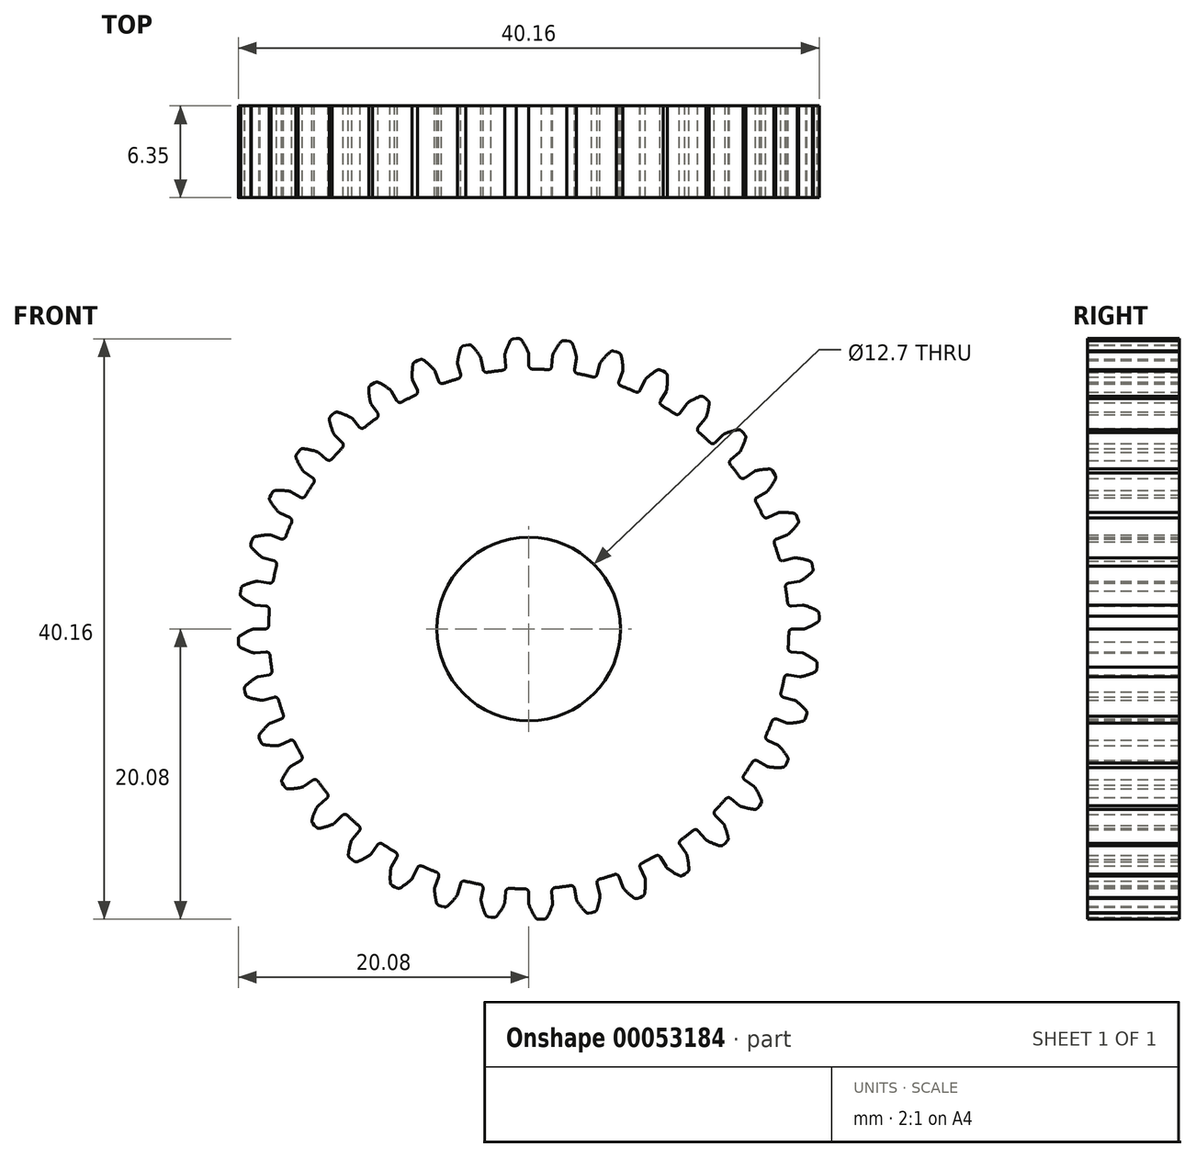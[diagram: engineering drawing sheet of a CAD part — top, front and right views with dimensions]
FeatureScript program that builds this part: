
annotation { "Feature Type Name" : "Feature", "Feature Type Description" : "" }
export const myFeature = defineFeature(function(context is Context, id is Id, definition is map)
    precondition{}
    {
        {
            var Q0;
            Q0=qCreatedBy(makeId("Front.planeOp"),FACE);
            var sketch = newSketch(context, id + "F0", { "sketchPlane" : qUnion([Q0])});
            skArc(sketch, "E0", {"start": v(-1.82, 17.9) * mm, "mid": v(-2.35, 17.83) * mm, "end": v(-2.88, 17.75) * mm});
            skLineSegment(sketch, "E1", {"start": v(0, 18.24) * mm, "end": v(0, 19.05) * mm, "construction": true});
            skLineSegment(sketch, "E2", {"start": v(0, 19) * mm, "end": v(0, 18.24) * mm});
            skLineSegment(sketch, "E3", {"start": v(-0.69, 20.08) * mm, "end": v(-0.88, 20.08) * mm});
            skArc(sketch, "E4.trimOffspring", {"start": v(-0.02, 19.1) * mm, "mid": v(-0.22, 19.54) * mm, "end": v(-0.47, 19.97) * mm});
            skPoint(sketch, "E5.visualSharp", {"position": v(-0.55, 20.08) * mm});
            skArc(sketch, "E5.filletArc", {"start": v(-0.47, 19.97) * mm, "mid": v(-0.56, 20.05) * mm, "end": v(-0.69, 20.08) * mm});
            skPoint(sketch, "E6.visualSharp", {"position": v(0, 19.05) * mm});
            skArc(sketch, "E6.filletArc", {"start": v(0, 19) * mm, "mid": v(0, 19.05) * mm, "end": v(-0.02, 19.1) * mm});
            skLineSegment(sketch, "E7.MirrorCS", {"start": v(-1.07, 20.07) * mm, "end": v(-0.88, 20.08) * mm});
            skLineSegment(sketch, "E8.MirrorCS", {"start": v(-1.66, 18.93) * mm, "end": v(-1.59, 18.17) * mm});
            skArc(sketch, "E9.MirrorCS", {"start": v(-1.66, 18.93) * mm, "mid": v(-1.66, 18.98) * mm, "end": v(-1.65, 19.02) * mm});
            skArc(sketch, "E10.MirrorCS", {"start": v(-1.65, 19.02) * mm, "mid": v(-1.48, 19.49) * mm, "end": v(-1.27, 19.93) * mm});
            skArc(sketch, "E11.MirrorCS", {"start": v(-1.27, 19.93) * mm, "mid": v(-1.18, 20.02) * mm, "end": v(-1.07, 20.07) * mm});
            skPoint(sketch, "E12.visualSharp", {"position": v(0, 17.98) * mm});
            skArc(sketch, "E12.filletArc", {"start": v(0, 18.24) * mm, "mid": v(0.07, 18.06) * mm, "end": v(0.25, 17.98) * mm});
            skPoint(sketch, "E13.visualSharp", {"position": v(-1.57, 17.91) * mm});
            skArc(sketch, "E13.filletArc", {"start": v(-1.82, 17.9) * mm, "mid": v(-1.65, 17.98) * mm, "end": v(-1.59, 18.17) * mm});
            skArc(sketch, "E14.1.0", {"start": v(-4.9, 17.3) * mm, "mid": v(-4.74, 17.42) * mm, "end": v(-4.72, 17.61) * mm});
            skLineSegment(sketch, "E14.1.1", {"start": v(-4.92, 18.35) * mm, "end": v(-4.72, 17.61) * mm});
            skArc(sketch, "E14.1.2", {"start": v(-4.92, 18.35) * mm, "mid": v(-4.93, 18.4) * mm, "end": v(-4.93, 18.45) * mm});
            skArc(sketch, "E14.1.3", {"start": v(-4.93, 18.45) * mm, "mid": v(-4.84, 18.94) * mm, "end": v(-4.71, 19.41) * mm});
            skArc(sketch, "E14.1.4", {"start": v(-4.71, 19.41) * mm, "mid": v(-4.64, 19.51) * mm, "end": v(-4.54, 19.58) * mm});
            skLineSegment(sketch, "E14.1.5", {"start": v(-4.54, 19.58) * mm, "end": v(-4.35, 19.62) * mm});
            skLineSegment(sketch, "E14.1.6", {"start": v(-4.16, 19.66) * mm, "end": v(-4.35, 19.62) * mm});
            skPoint(sketch, "E14.1.7", {"position": v(-4.03, 19.68) * mm});
            skArc(sketch, "E14.1.8", {"start": v(-3.93, 19.58) * mm, "mid": v(-4.04, 19.65) * mm, "end": v(-4.16, 19.66) * mm});
            skArc(sketch, "E14.1.9", {"start": v(-3.33, 18.8) * mm, "mid": v(-3.61, 19.2) * mm, "end": v(-3.93, 19.58) * mm});
            skArc(sketch, "E14.1.10", {"start": v(-3.3, 18.71) * mm, "mid": v(-3.31, 18.76) * mm, "end": v(-3.33, 18.8) * mm});
            skLineSegment(sketch, "E14.1.11", {"start": v(-3.3, 18.71) * mm, "end": v(-3.17, 17.96) * mm});
            skArc(sketch, "E14.1.12", {"start": v(-3.17, 17.96) * mm, "mid": v(-3.06, 17.8) * mm, "end": v(-2.88, 17.75) * mm});
            skArc(sketch, "E14.2.0", {"start": v(-7.83, 16.2) * mm, "mid": v(-7.7, 16.33) * mm, "end": v(-7.7, 16.53) * mm});
            skLineSegment(sketch, "E14.2.1", {"start": v(-8.03, 17.22) * mm, "end": v(-7.7, 16.53) * mm});
            skArc(sketch, "E14.2.2", {"start": v(-8.03, 17.22) * mm, "mid": v(-8.05, 17.27) * mm, "end": v(-8.05, 17.31) * mm});
            skArc(sketch, "E14.2.3", {"start": v(-8.05, 17.31) * mm, "mid": v(-8.06, 17.8) * mm, "end": v(-8, 18.3) * mm});
            skArc(sketch, "E14.2.4", {"start": v(-8, 18.3) * mm, "mid": v(-7.96, 18.41) * mm, "end": v(-7.87, 18.5) * mm});
            skLineSegment(sketch, "E14.2.5", {"start": v(-7.87, 18.5) * mm, "end": v(-7.7, 18.57) * mm});
            skLineSegment(sketch, "E14.2.6", {"start": v(-7.51, 18.64) * mm, "end": v(-7.7, 18.57) * mm});
            skPoint(sketch, "E14.2.7", {"position": v(-7.39, 18.68) * mm});
            skArc(sketch, "E14.2.8", {"start": v(-7.27, 18.6) * mm, "mid": v(-7.39, 18.65) * mm, "end": v(-7.51, 18.64) * mm});
            skArc(sketch, "E14.2.9", {"start": v(-6.55, 17.94) * mm, "mid": v(-6.9, 18.29) * mm, "end": v(-7.27, 18.6) * mm});
            skArc(sketch, "E14.2.10", {"start": v(-6.5, 17.86) * mm, "mid": v(-6.52, 17.9) * mm, "end": v(-6.55, 17.94) * mm});
            skLineSegment(sketch, "E14.2.11", {"start": v(-6.5, 17.86) * mm, "end": v(-6.24, 17.14) * mm});
            skArc(sketch, "E14.2.12", {"start": v(-6.24, 17.14) * mm, "mid": v(-6.1, 17) * mm, "end": v(-5.91, 16.98) * mm});
            skArc(sketch, "E15.2.3.0", {"start": v(-10.52, 14.59) * mm, "mid": v(-10.42, 14.75) * mm, "end": v(-10.46, 14.94) * mm});
            skLineSegment(sketch, "E15.4.3.0", {"start": v(-10.9, 15.57) * mm, "end": v(-10.46, 14.94) * mm});
            skArc(sketch, "E15.7.3.0", {"start": v(-10.9, 15.57) * mm, "mid": v(-10.92, 15.6) * mm, "end": v(-10.94, 15.65) * mm});
            skArc(sketch, "E15.11.3.0", {"start": v(-10.94, 15.65) * mm, "mid": v(-11.03, 16.14) * mm, "end": v(-11.07, 16.63) * mm});
            skArc(sketch, "E15.15.3.0", {"start": v(-11.07, 16.63) * mm, "mid": v(-11.04, 16.75) * mm, "end": v(-10.96, 16.84) * mm});
            skLineSegment(sketch, "E15.19.3.0", {"start": v(-10.96, 16.84) * mm, "end": v(-10.8, 16.95) * mm});
            skLineSegment(sketch, "E15.22.3.0", {"start": v(-10.63, 17.05) * mm, "end": v(-10.8, 16.95) * mm});
            skPoint(sketch, "E15.25.3.0", {"position": v(-10.52, 17.12) * mm});
            skArc(sketch, "E15.26.3.0", {"start": v(-10.4, 17.06) * mm, "mid": v(-10.52, 17.08) * mm, "end": v(-10.63, 17.05) * mm});
            skArc(sketch, "E15.30.3.0", {"start": v(-9.56, 16.53) * mm, "mid": v(-9.97, 16.81) * mm, "end": v(-10.4, 17.06) * mm});
            skArc(sketch, "E15.34.3.0", {"start": v(-9.5, 16.46) * mm, "mid": v(-9.53, 16.5) * mm, "end": v(-9.56, 16.53) * mm});
            skLineSegment(sketch, "E15.38.3.0", {"start": v(-9.5, 16.46) * mm, "end": v(-9.12, 15.8) * mm});
            skArc(sketch, "E15.41.3.0", {"start": v(-9.12, 15.8) * mm, "mid": v(-8.97, 15.67) * mm, "end": v(-8.77, 15.7) * mm});
            skArc(sketch, "E15.2.4.0", {"start": v(-12.9, 12.54) * mm, "mid": v(-12.82, 12.72) * mm, "end": v(-12.9, 12.9) * mm});
            skLineSegment(sketch, "E15.4.4.0", {"start": v(-13.44, 13.44) * mm, "end": v(-12.9, 12.9) * mm});
            skArc(sketch, "E15.7.4.0", {"start": v(-13.44, 13.44) * mm, "mid": v(-13.47, 13.47) * mm, "end": v(-13.5, 13.52) * mm});
            skArc(sketch, "E15.11.4.0", {"start": v(-13.5, 13.52) * mm, "mid": v(-13.66, 13.98) * mm, "end": v(-13.78, 14.45) * mm});
            skArc(sketch, "E15.15.4.0", {"start": v(-13.78, 14.45) * mm, "mid": v(-13.78, 14.58) * mm, "end": v(-13.72, 14.68) * mm});
            skLineSegment(sketch, "E15.19.4.0", {"start": v(-13.72, 14.68) * mm, "end": v(-13.58, 14.82) * mm});
            skLineSegment(sketch, "E15.22.4.0", {"start": v(-13.43, 14.94) * mm, "end": v(-13.58, 14.82) * mm});
            skPoint(sketch, "E15.25.4.0", {"position": v(-13.33, 15.03) * mm});
            skArc(sketch, "E15.26.4.0", {"start": v(-13.2, 15) * mm, "mid": v(-13.32, 15) * mm, "end": v(-13.43, 14.94) * mm});
            skArc(sketch, "E15.30.4.0", {"start": v(-12.29, 14.62) * mm, "mid": v(-12.73, 14.83) * mm, "end": v(-13.2, 15) * mm});
            skArc(sketch, "E15.34.4.0", {"start": v(-12.21, 14.56) * mm, "mid": v(-12.25, 14.6) * mm, "end": v(-12.29, 14.62) * mm});
            skLineSegment(sketch, "E15.38.4.0", {"start": v(-12.21, 14.56) * mm, "end": v(-11.72, 13.97) * mm});
            skArc(sketch, "E15.41.4.0", {"start": v(-11.72, 13.97) * mm, "mid": v(-11.55, 13.88) * mm, "end": v(-11.37, 13.94) * mm});
            skArc(sketch, "E15.2.5.0", {"start": v(-14.87, 10.1) * mm, "mid": v(-14.83, 10.3) * mm, "end": v(-14.94, 10.46) * mm});
            skLineSegment(sketch, "E15.4.5.0", {"start": v(-15.57, 10.9) * mm, "end": v(-14.94, 10.46) * mm});
            skArc(sketch, "E15.7.5.0", {"start": v(-15.57, 10.9) * mm, "mid": v(-15.6, 10.93) * mm, "end": v(-15.63, 10.97) * mm});
            skArc(sketch, "E15.11.5.0", {"start": v(-15.63, 10.97) * mm, "mid": v(-15.88, 11.4) * mm, "end": v(-16.09, 11.84) * mm});
            skArc(sketch, "E15.15.5.0", {"start": v(-16.09, 11.84) * mm, "mid": v(-16.1, 11.96) * mm, "end": v(-16.06, 12.08) * mm});
            skLineSegment(sketch, "E15.19.5.0", {"start": v(-16.06, 12.08) * mm, "end": v(-15.95, 12.24) * mm});
            skLineSegment(sketch, "E15.22.5.0", {"start": v(-15.82, 12.38) * mm, "end": v(-15.95, 12.24) * mm});
            skPoint(sketch, "E15.25.5.0", {"position": v(-15.74, 12.49) * mm});
            skArc(sketch, "E15.26.5.0", {"start": v(-15.6, 12.47) * mm, "mid": v(-15.72, 12.46) * mm, "end": v(-15.82, 12.38) * mm});
            skArc(sketch, "E15.30.5.0", {"start": v(-14.64, 12.26) * mm, "mid": v(-15.11, 12.4) * mm, "end": v(-15.6, 12.47) * mm});
            skArc(sketch, "E15.34.5.0", {"start": v(-14.56, 12.21) * mm, "mid": v(-14.6, 12.24) * mm, "end": v(-14.64, 12.26) * mm});
            skLineSegment(sketch, "E15.38.5.0", {"start": v(-14.56, 12.21) * mm, "end": v(-13.97, 11.72) * mm});
            skArc(sketch, "E15.41.5.0", {"start": v(-13.97, 11.72) * mm, "mid": v(-13.79, 11.66) * mm, "end": v(-13.61, 11.75) * mm});
            skArc(sketch, "E15.2.6.0", {"start": v(-16.4, 7.37) * mm, "mid": v(-16.4, 7.56) * mm, "end": v(-16.53, 7.7) * mm});
            skLineSegment(sketch, "E15.4.6.0", {"start": v(-17.22, 8.03) * mm, "end": v(-16.53, 7.7) * mm});
            skArc(sketch, "E15.7.6.0", {"start": v(-17.22, 8.03) * mm, "mid": v(-17.26, 8.05) * mm, "end": v(-17.3, 8.09) * mm});
            skArc(sketch, "E15.11.6.0", {"start": v(-17.3, 8.09) * mm, "mid": v(-17.62, 8.46) * mm, "end": v(-17.9, 8.87) * mm});
            skArc(sketch, "E15.15.6.0", {"start": v(-17.9, 8.87) * mm, "mid": v(-17.93, 8.99) * mm, "end": v(-17.91, 9.1) * mm});
            skLineSegment(sketch, "E15.19.6.0", {"start": v(-17.91, 9.1) * mm, "end": v(-17.83, 9.28) * mm});
            skLineSegment(sketch, "E15.22.6.0", {"start": v(-17.73, 9.45) * mm, "end": v(-17.83, 9.28) * mm});
            skPoint(sketch, "E15.25.6.0", {"position": v(-17.67, 9.56) * mm});
            skArc(sketch, "E15.26.6.0", {"start": v(-17.53, 9.57) * mm, "mid": v(-17.65, 9.54) * mm, "end": v(-17.73, 9.45) * mm});
            skArc(sketch, "E15.30.6.0", {"start": v(-16.55, 9.53) * mm, "mid": v(-17.04, 9.58) * mm, "end": v(-17.53, 9.57) * mm});
            skArc(sketch, "E15.34.6.0", {"start": v(-16.46, 9.5) * mm, "mid": v(-16.5, 9.52) * mm, "end": v(-16.55, 9.53) * mm});
            skLineSegment(sketch, "E15.38.6.0", {"start": v(-16.46, 9.5) * mm, "end": v(-15.8, 9.12) * mm});
            skArc(sketch, "E15.41.6.0", {"start": v(-15.8, 9.12) * mm, "mid": v(-15.6, 9.1) * mm, "end": v(-15.45, 9.2) * mm});
            skArc(sketch, "E15.2.7.0", {"start": v(-17.43, 4.41) * mm, "mid": v(-17.46, 4.6) * mm, "end": v(-17.61, 4.72) * mm});
            skLineSegment(sketch, "E15.4.7.0", {"start": v(-18.35, 4.92) * mm, "end": v(-17.61, 4.72) * mm});
            skArc(sketch, "E15.7.7.0", {"start": v(-18.35, 4.92) * mm, "mid": v(-18.4, 4.93) * mm, "end": v(-18.44, 4.96) * mm});
            skArc(sketch, "E15.11.7.0", {"start": v(-18.44, 4.96) * mm, "mid": v(-18.82, 5.27) * mm, "end": v(-19.17, 5.63) * mm});
            skArc(sketch, "E15.15.7.0", {"start": v(-19.17, 5.63) * mm, "mid": v(-19.22, 5.74) * mm, "end": v(-19.22, 5.86) * mm});
            skLineSegment(sketch, "E15.19.7.0", {"start": v(-19.22, 5.86) * mm, "end": v(-19.17, 6.04) * mm});
            skLineSegment(sketch, "E15.22.7.0", {"start": v(-19.1, 6.22) * mm, "end": v(-19.17, 6.04) * mm});
            skPoint(sketch, "E15.25.7.0", {"position": v(-19.06, 6.35) * mm});
            skArc(sketch, "E15.26.7.0", {"start": v(-18.93, 6.38) * mm, "mid": v(-19.04, 6.33) * mm, "end": v(-19.1, 6.22) * mm});
            skArc(sketch, "E15.30.7.0", {"start": v(-17.95, 6.51) * mm, "mid": v(-18.44, 6.47) * mm, "end": v(-18.93, 6.38) * mm});
            skArc(sketch, "E15.34.7.0", {"start": v(-17.86, 6.5) * mm, "mid": v(-17.9, 6.51) * mm, "end": v(-17.95, 6.51) * mm});
            skLineSegment(sketch, "E15.38.7.0", {"start": v(-17.86, 6.5) * mm, "end": v(-17.14, 6.24) * mm});
            skArc(sketch, "E15.41.7.0", {"start": v(-17.14, 6.24) * mm, "mid": v(-16.94, 6.24) * mm, "end": v(-16.81, 6.39) * mm});
            skArc(sketch, "E15.2.8.0", {"start": v(-17.93, 1.32) * mm, "mid": v(-18, 1.5) * mm, "end": v(-18.17, 1.59) * mm});
            skLineSegment(sketch, "E15.4.8.0", {"start": v(-18.93, 1.66) * mm, "end": v(-18.17, 1.59) * mm});
            skArc(sketch, "E15.7.8.0", {"start": v(-18.93, 1.66) * mm, "mid": v(-18.98, 1.66) * mm, "end": v(-19.02, 1.68) * mm});
            skArc(sketch, "E15.11.8.0", {"start": v(-19.02, 1.68) * mm, "mid": v(-19.45, 1.93) * mm, "end": v(-19.85, 2.21) * mm});
            skArc(sketch, "E15.15.8.0", {"start": v(-19.85, 2.21) * mm, "mid": v(-19.93, 2.31) * mm, "end": v(-19.95, 2.43) * mm});
            skLineSegment(sketch, "E15.19.8.0", {"start": v(-19.95, 2.43) * mm, "end": v(-19.93, 2.62) * mm});
            skLineSegment(sketch, "E15.22.8.0", {"start": v(-19.9, 2.81) * mm, "end": v(-19.93, 2.62) * mm});
            skPoint(sketch, "E15.25.8.0", {"position": v(-19.87, 2.94) * mm});
            skArc(sketch, "E15.26.8.0", {"start": v(-19.75, 3) * mm, "mid": v(-19.85, 2.93) * mm, "end": v(-19.9, 2.81) * mm});
            skArc(sketch, "E15.30.8.0", {"start": v(-18.8, 3.3) * mm, "mid": v(-19.29, 3.17) * mm, "end": v(-19.75, 3) * mm});
            skArc(sketch, "E15.34.8.0", {"start": v(-18.71, 3.3) * mm, "mid": v(-18.76, 3.3) * mm, "end": v(-18.8, 3.3) * mm});
            skLineSegment(sketch, "E15.38.8.0", {"start": v(-18.71, 3.3) * mm, "end": v(-17.96, 3.17) * mm});
            skArc(sketch, "E15.41.8.0", {"start": v(-17.96, 3.17) * mm, "mid": v(-17.77, 3.2) * mm, "end": v(-17.66, 3.37) * mm});
            skArc(sketch, "E15.2.9.0", {"start": v(-17.9, -1.82) * mm, "mid": v(-17.98, -1.65) * mm, "end": v(-18.17, -1.59) * mm});
            skLineSegment(sketch, "E15.4.9.0", {"start": v(-18.93, -1.66) * mm, "end": v(-18.17, -1.59) * mm});
            skArc(sketch, "E15.7.9.0", {"start": v(-18.93, -1.66) * mm, "mid": v(-18.98, -1.66) * mm, "end": v(-19.02, -1.65) * mm});
            skArc(sketch, "E15.11.9.0", {"start": v(-19.02, -1.65) * mm, "mid": v(-19.49, -1.48) * mm, "end": v(-19.93, -1.27) * mm});
            skArc(sketch, "E15.15.9.0", {"start": v(-19.93, -1.27) * mm, "mid": v(-20.02, -1.18) * mm, "end": v(-20.07, -1.07) * mm});
            skLineSegment(sketch, "E15.19.9.0", {"start": v(-20.07, -1.07) * mm, "end": v(-20.08, -0.88) * mm});
            skLineSegment(sketch, "E15.22.9.0", {"start": v(-20.08, -0.69) * mm, "end": v(-20.08, -0.88) * mm});
            skPoint(sketch, "E15.25.9.0", {"position": v(-20.08, -0.55) * mm});
            skArc(sketch, "E15.26.9.0", {"start": v(-19.97, -0.47) * mm, "mid": v(-20.05, -0.56) * mm, "end": v(-20.08, -0.69) * mm});
            skArc(sketch, "E15.30.9.0", {"start": v(-19.1, -0.02) * mm, "mid": v(-19.54, -0.22) * mm, "end": v(-19.97, -0.47) * mm});
            skArc(sketch, "E15.34.9.0", {"start": v(-19, 0) * mm, "mid": v(-19.05, 0) * mm, "end": v(-19.1, -0.02) * mm});
            skLineSegment(sketch, "E15.38.9.0", {"start": v(-19, 0) * mm, "end": v(-18.24, 0) * mm});
            skArc(sketch, "E15.41.9.0", {"start": v(-18.24, 0) * mm, "mid": v(-18.06, 0.07) * mm, "end": v(-17.98, 0.25) * mm});
            skArc(sketch, "E15.2.10.0", {"start": v(-17.3, -4.9) * mm, "mid": v(-17.42, -4.74) * mm, "end": v(-17.61, -4.72) * mm});
            skLineSegment(sketch, "E15.4.10.0", {"start": v(-18.35, -4.92) * mm, "end": v(-17.61, -4.72) * mm});
            skArc(sketch, "E15.7.10.0", {"start": v(-18.35, -4.92) * mm, "mid": v(-18.4, -4.93) * mm, "end": v(-18.45, -4.93) * mm});
            skArc(sketch, "E15.11.10.0", {"start": v(-18.45, -4.93) * mm, "mid": v(-18.94, -4.84) * mm, "end": v(-19.41, -4.71) * mm});
            skArc(sketch, "E15.15.10.0", {"start": v(-19.41, -4.71) * mm, "mid": v(-19.51, -4.64) * mm, "end": v(-19.58, -4.54) * mm});
            skLineSegment(sketch, "E15.19.10.0", {"start": v(-19.58, -4.54) * mm, "end": v(-19.62, -4.35) * mm});
            skLineSegment(sketch, "E15.22.10.0", {"start": v(-19.66, -4.16) * mm, "end": v(-19.62, -4.35) * mm});
            skPoint(sketch, "E15.25.10.0", {"position": v(-19.68, -4.03) * mm});
            skArc(sketch, "E15.26.10.0", {"start": v(-19.58, -3.93) * mm, "mid": v(-19.65, -4.04) * mm, "end": v(-19.66, -4.16) * mm});
            skArc(sketch, "E15.30.10.0", {"start": v(-18.8, -3.33) * mm, "mid": v(-19.2, -3.61) * mm, "end": v(-19.58, -3.93) * mm});
            skArc(sketch, "E15.34.10.0", {"start": v(-18.71, -3.3) * mm, "mid": v(-18.76, -3.31) * mm, "end": v(-18.8, -3.33) * mm});
            skLineSegment(sketch, "E15.38.10.0", {"start": v(-18.71, -3.3) * mm, "end": v(-17.96, -3.17) * mm});
            skArc(sketch, "E15.41.10.0", {"start": v(-17.96, -3.17) * mm, "mid": v(-17.8, -3.06) * mm, "end": v(-17.75, -2.88) * mm});
            skArc(sketch, "E15.2.11.0", {"start": v(-16.2, -7.83) * mm, "mid": v(-16.33, -7.7) * mm, "end": v(-16.53, -7.7) * mm});
            skLineSegment(sketch, "E15.4.11.0", {"start": v(-17.22, -8.03) * mm, "end": v(-16.53, -7.7) * mm});
            skArc(sketch, "E15.7.11.0", {"start": v(-17.22, -8.03) * mm, "mid": v(-17.27, -8.05) * mm, "end": v(-17.31, -8.05) * mm});
            skArc(sketch, "E15.11.11.0", {"start": v(-17.31, -8.05) * mm, "mid": v(-17.8, -8.06) * mm, "end": v(-18.3, -8) * mm});
            skArc(sketch, "E15.15.11.0", {"start": v(-18.3, -8) * mm, "mid": v(-18.41, -7.96) * mm, "end": v(-18.5, -7.87) * mm});
            skLineSegment(sketch, "E15.19.11.0", {"start": v(-18.5, -7.87) * mm, "end": v(-18.57, -7.7) * mm});
            skLineSegment(sketch, "E15.22.11.0", {"start": v(-18.64, -7.51) * mm, "end": v(-18.57, -7.7) * mm});
            skPoint(sketch, "E15.25.11.0", {"position": v(-18.68, -7.39) * mm});
            skArc(sketch, "E15.26.11.0", {"start": v(-18.6, -7.27) * mm, "mid": v(-18.65, -7.39) * mm, "end": v(-18.64, -7.51) * mm});
            skArc(sketch, "E15.30.11.0", {"start": v(-17.94, -6.55) * mm, "mid": v(-18.29, -6.9) * mm, "end": v(-18.6, -7.27) * mm});
            skArc(sketch, "E15.34.11.0", {"start": v(-17.86, -6.5) * mm, "mid": v(-17.9, -6.52) * mm, "end": v(-17.94, -6.55) * mm});
            skLineSegment(sketch, "E15.38.11.0", {"start": v(-17.86, -6.5) * mm, "end": v(-17.14, -6.24) * mm});
            skArc(sketch, "E15.41.11.0", {"start": v(-17.14, -6.24) * mm, "mid": v(-17, -6.1) * mm, "end": v(-16.98, -5.91) * mm});
            skArc(sketch, "E15.2.12.0", {"start": v(-14.59, -10.52) * mm, "mid": v(-14.75, -10.42) * mm, "end": v(-14.94, -10.46) * mm});
            skLineSegment(sketch, "E15.4.12.0", {"start": v(-15.57, -10.9) * mm, "end": v(-14.94, -10.46) * mm});
            skArc(sketch, "E15.7.12.0", {"start": v(-15.57, -10.9) * mm, "mid": v(-15.6, -10.92) * mm, "end": v(-15.65, -10.94) * mm});
            skArc(sketch, "E15.11.12.0", {"start": v(-15.65, -10.94) * mm, "mid": v(-16.14, -11.03) * mm, "end": v(-16.63, -11.07) * mm});
            skArc(sketch, "E15.15.12.0", {"start": v(-16.63, -11.07) * mm, "mid": v(-16.75, -11.04) * mm, "end": v(-16.84, -10.96) * mm});
            skLineSegment(sketch, "E15.19.12.0", {"start": v(-16.84, -10.96) * mm, "end": v(-16.95, -10.8) * mm});
            skLineSegment(sketch, "E15.22.12.0", {"start": v(-17.05, -10.63) * mm, "end": v(-16.95, -10.8) * mm});
            skPoint(sketch, "E15.25.12.0", {"position": v(-17.12, -10.52) * mm});
            skArc(sketch, "E15.26.12.0", {"start": v(-17.06, -10.4) * mm, "mid": v(-17.08, -10.52) * mm, "end": v(-17.05, -10.63) * mm});
            skArc(sketch, "E15.30.12.0", {"start": v(-16.53, -9.56) * mm, "mid": v(-16.81, -9.97) * mm, "end": v(-17.06, -10.4) * mm});
            skArc(sketch, "E15.34.12.0", {"start": v(-16.46, -9.5) * mm, "mid": v(-16.5, -9.53) * mm, "end": v(-16.53, -9.56) * mm});
            skLineSegment(sketch, "E15.38.12.0", {"start": v(-16.46, -9.5) * mm, "end": v(-15.8, -9.12) * mm});
            skArc(sketch, "E15.41.12.0", {"start": v(-15.8, -9.12) * mm, "mid": v(-15.67, -8.97) * mm, "end": v(-15.7, -8.77) * mm});
            skArc(sketch, "E15.2.13.0", {"start": v(-12.54, -12.9) * mm, "mid": v(-12.72, -12.82) * mm, "end": v(-12.9, -12.9) * mm});
            skLineSegment(sketch, "E15.4.13.0", {"start": v(-13.44, -13.44) * mm, "end": v(-12.9, -12.9) * mm});
            skArc(sketch, "E15.7.13.0", {"start": v(-13.44, -13.44) * mm, "mid": v(-13.47, -13.47) * mm, "end": v(-13.52, -13.5) * mm});
            skArc(sketch, "E15.11.13.0", {"start": v(-13.52, -13.5) * mm, "mid": v(-13.98, -13.66) * mm, "end": v(-14.45, -13.78) * mm});
            skArc(sketch, "E15.15.13.0", {"start": v(-14.45, -13.78) * mm, "mid": v(-14.58, -13.78) * mm, "end": v(-14.68, -13.72) * mm});
            skLineSegment(sketch, "E15.19.13.0", {"start": v(-14.68, -13.72) * mm, "end": v(-14.82, -13.58) * mm});
            skLineSegment(sketch, "E15.22.13.0", {"start": v(-14.94, -13.43) * mm, "end": v(-14.82, -13.58) * mm});
            skPoint(sketch, "E15.25.13.0", {"position": v(-15.03, -13.33) * mm});
            skArc(sketch, "E15.26.13.0", {"start": v(-15, -13.2) * mm, "mid": v(-15, -13.32) * mm, "end": v(-14.94, -13.43) * mm});
            skArc(sketch, "E15.30.13.0", {"start": v(-14.62, -12.29) * mm, "mid": v(-14.83, -12.73) * mm, "end": v(-15, -13.2) * mm});
            skArc(sketch, "E15.34.13.0", {"start": v(-14.56, -12.21) * mm, "mid": v(-14.6, -12.25) * mm, "end": v(-14.62, -12.29) * mm});
            skLineSegment(sketch, "E15.38.13.0", {"start": v(-14.56, -12.21) * mm, "end": v(-13.97, -11.72) * mm});
            skArc(sketch, "E15.41.13.0", {"start": v(-13.97, -11.72) * mm, "mid": v(-13.88, -11.55) * mm, "end": v(-13.94, -11.37) * mm});
            skArc(sketch, "E15.2.14.0", {"start": v(-10.1, -14.87) * mm, "mid": v(-10.3, -14.83) * mm, "end": v(-10.46, -14.94) * mm});
            skLineSegment(sketch, "E15.4.14.0", {"start": v(-10.9, -15.57) * mm, "end": v(-10.46, -14.94) * mm});
            skArc(sketch, "E15.7.14.0", {"start": v(-10.9, -15.57) * mm, "mid": v(-10.93, -15.6) * mm, "end": v(-10.97, -15.63) * mm});
            skArc(sketch, "E15.11.14.0", {"start": v(-10.97, -15.63) * mm, "mid": v(-11.4, -15.88) * mm, "end": v(-11.84, -16.09) * mm});
            skArc(sketch, "E15.15.14.0", {"start": v(-11.84, -16.09) * mm, "mid": v(-11.96, -16.1) * mm, "end": v(-12.08, -16.06) * mm});
            skLineSegment(sketch, "E15.19.14.0", {"start": v(-12.08, -16.06) * mm, "end": v(-12.24, -15.95) * mm});
            skLineSegment(sketch, "E15.22.14.0", {"start": v(-12.38, -15.82) * mm, "end": v(-12.24, -15.95) * mm});
            skPoint(sketch, "E15.25.14.0", {"position": v(-12.49, -15.74) * mm});
            skArc(sketch, "E15.26.14.0", {"start": v(-12.47, -15.6) * mm, "mid": v(-12.46, -15.72) * mm, "end": v(-12.38, -15.82) * mm});
            skArc(sketch, "E15.30.14.0", {"start": v(-12.26, -14.64) * mm, "mid": v(-12.4, -15.11) * mm, "end": v(-12.47, -15.6) * mm});
            skArc(sketch, "E15.34.14.0", {"start": v(-12.21, -14.56) * mm, "mid": v(-12.24, -14.6) * mm, "end": v(-12.26, -14.64) * mm});
            skLineSegment(sketch, "E15.38.14.0", {"start": v(-12.21, -14.56) * mm, "end": v(-11.72, -13.97) * mm});
            skArc(sketch, "E15.41.14.0", {"start": v(-11.72, -13.97) * mm, "mid": v(-11.66, -13.79) * mm, "end": v(-11.75, -13.61) * mm});
            skArc(sketch, "E15.2.15.0", {"start": v(-7.37, -16.4) * mm, "mid": v(-7.56, -16.4) * mm, "end": v(-7.7, -16.53) * mm});
            skLineSegment(sketch, "E15.4.15.0", {"start": v(-8.03, -17.22) * mm, "end": v(-7.7, -16.53) * mm});
            skArc(sketch, "E15.7.15.0", {"start": v(-8.03, -17.22) * mm, "mid": v(-8.05, -17.26) * mm, "end": v(-8.09, -17.3) * mm});
            skArc(sketch, "E15.11.15.0", {"start": v(-8.09, -17.3) * mm, "mid": v(-8.46, -17.62) * mm, "end": v(-8.87, -17.9) * mm});
            skArc(sketch, "E15.15.15.0", {"start": v(-8.87, -17.9) * mm, "mid": v(-8.99, -17.93) * mm, "end": v(-9.1, -17.91) * mm});
            skLineSegment(sketch, "E15.19.15.0", {"start": v(-9.1, -17.91) * mm, "end": v(-9.28, -17.83) * mm});
            skLineSegment(sketch, "E15.22.15.0", {"start": v(-9.45, -17.73) * mm, "end": v(-9.28, -17.83) * mm});
            skPoint(sketch, "E15.25.15.0", {"position": v(-9.56, -17.67) * mm});
            skArc(sketch, "E15.26.15.0", {"start": v(-9.57, -17.53) * mm, "mid": v(-9.54, -17.65) * mm, "end": v(-9.45, -17.73) * mm});
            skArc(sketch, "E15.30.15.0", {"start": v(-9.53, -16.55) * mm, "mid": v(-9.58, -17.04) * mm, "end": v(-9.57, -17.53) * mm});
            skArc(sketch, "E15.34.15.0", {"start": v(-9.5, -16.46) * mm, "mid": v(-9.52, -16.5) * mm, "end": v(-9.53, -16.55) * mm});
            skLineSegment(sketch, "E15.38.15.0", {"start": v(-9.5, -16.46) * mm, "end": v(-9.12, -15.8) * mm});
            skArc(sketch, "E15.41.15.0", {"start": v(-9.12, -15.8) * mm, "mid": v(-9.1, -15.6) * mm, "end": v(-9.2, -15.45) * mm});
            skArc(sketch, "E15.2.16.0", {"start": v(-4.41, -17.43) * mm, "mid": v(-4.6, -17.46) * mm, "end": v(-4.72, -17.61) * mm});
            skLineSegment(sketch, "E15.4.16.0", {"start": v(-4.92, -18.35) * mm, "end": v(-4.72, -17.61) * mm});
            skArc(sketch, "E15.7.16.0", {"start": v(-4.92, -18.35) * mm, "mid": v(-4.93, -18.4) * mm, "end": v(-4.96, -18.44) * mm});
            skArc(sketch, "E15.11.16.0", {"start": v(-4.96, -18.44) * mm, "mid": v(-5.27, -18.82) * mm, "end": v(-5.63, -19.17) * mm});
            skArc(sketch, "E15.15.16.0", {"start": v(-5.63, -19.17) * mm, "mid": v(-5.74, -19.22) * mm, "end": v(-5.86, -19.22) * mm});
            skLineSegment(sketch, "E15.19.16.0", {"start": v(-5.86, -19.22) * mm, "end": v(-6.04, -19.17) * mm});
            skLineSegment(sketch, "E15.22.16.0", {"start": v(-6.22, -19.1) * mm, "end": v(-6.04, -19.17) * mm});
            skPoint(sketch, "E15.25.16.0", {"position": v(-6.35, -19.06) * mm});
            skArc(sketch, "E15.26.16.0", {"start": v(-6.38, -18.93) * mm, "mid": v(-6.33, -19.04) * mm, "end": v(-6.22, -19.1) * mm});
            skArc(sketch, "E15.30.16.0", {"start": v(-6.51, -17.95) * mm, "mid": v(-6.47, -18.44) * mm, "end": v(-6.38, -18.93) * mm});
            skArc(sketch, "E15.34.16.0", {"start": v(-6.5, -17.86) * mm, "mid": v(-6.51, -17.9) * mm, "end": v(-6.51, -17.95) * mm});
            skLineSegment(sketch, "E15.38.16.0", {"start": v(-6.5, -17.86) * mm, "end": v(-6.24, -17.14) * mm});
            skArc(sketch, "E15.41.16.0", {"start": v(-6.24, -17.14) * mm, "mid": v(-6.24, -16.94) * mm, "end": v(-6.39, -16.81) * mm});
            skArc(sketch, "E15.2.17.0", {"start": v(-1.32, -17.93) * mm, "mid": v(-1.5, -18) * mm, "end": v(-1.59, -18.17) * mm});
            skLineSegment(sketch, "E15.4.17.0", {"start": v(-1.66, -18.93) * mm, "end": v(-1.59, -18.17) * mm});
            skArc(sketch, "E15.7.17.0", {"start": v(-1.66, -18.93) * mm, "mid": v(-1.66, -18.98) * mm, "end": v(-1.68, -19.02) * mm});
            skArc(sketch, "E15.11.17.0", {"start": v(-1.68, -19.02) * mm, "mid": v(-1.93, -19.45) * mm, "end": v(-2.21, -19.85) * mm});
            skArc(sketch, "E15.15.17.0", {"start": v(-2.21, -19.85) * mm, "mid": v(-2.31, -19.93) * mm, "end": v(-2.43, -19.95) * mm});
            skLineSegment(sketch, "E15.19.17.0", {"start": v(-2.43, -19.95) * mm, "end": v(-2.62, -19.93) * mm});
            skLineSegment(sketch, "E15.22.17.0", {"start": v(-2.81, -19.9) * mm, "end": v(-2.62, -19.93) * mm});
            skPoint(sketch, "E15.25.17.0", {"position": v(-2.94, -19.87) * mm});
            skArc(sketch, "E15.26.17.0", {"start": v(-3, -19.75) * mm, "mid": v(-2.93, -19.85) * mm, "end": v(-2.81, -19.9) * mm});
            skArc(sketch, "E15.30.17.0", {"start": v(-3.3, -18.8) * mm, "mid": v(-3.17, -19.29) * mm, "end": v(-3, -19.75) * mm});
            skArc(sketch, "E15.34.17.0", {"start": v(-3.3, -18.71) * mm, "mid": v(-3.3, -18.76) * mm, "end": v(-3.3, -18.8) * mm});
            skLineSegment(sketch, "E15.38.17.0", {"start": v(-3.3, -18.71) * mm, "end": v(-3.17, -17.96) * mm});
            skArc(sketch, "E15.41.17.0", {"start": v(-3.17, -17.96) * mm, "mid": v(-3.2, -17.77) * mm, "end": v(-3.37, -17.66) * mm});
            skArc(sketch, "E15.2.18.0", {"start": v(1.82, -17.9) * mm, "mid": v(1.65, -17.98) * mm, "end": v(1.59, -18.17) * mm});
            skLineSegment(sketch, "E15.4.18.0", {"start": v(1.66, -18.93) * mm, "end": v(1.59, -18.17) * mm});
            skArc(sketch, "E15.7.18.0", {"start": v(1.66, -18.93) * mm, "mid": v(1.66, -18.98) * mm, "end": v(1.65, -19.02) * mm});
            skArc(sketch, "E15.11.18.0", {"start": v(1.65, -19.02) * mm, "mid": v(1.48, -19.49) * mm, "end": v(1.27, -19.93) * mm});
            skArc(sketch, "E15.15.18.0", {"start": v(1.27, -19.93) * mm, "mid": v(1.18, -20.02) * mm, "end": v(1.07, -20.07) * mm});
            skLineSegment(sketch, "E15.19.18.0", {"start": v(1.07, -20.07) * mm, "end": v(0.88, -20.08) * mm});
            skLineSegment(sketch, "E15.22.18.0", {"start": v(0.69, -20.08) * mm, "end": v(0.88, -20.08) * mm});
            skPoint(sketch, "E15.25.18.0", {"position": v(0.55, -20.08) * mm});
            skArc(sketch, "E15.26.18.0", {"start": v(0.47, -19.97) * mm, "mid": v(0.56, -20.05) * mm, "end": v(0.69, -20.08) * mm});
            skArc(sketch, "E15.30.18.0", {"start": v(0.02, -19.1) * mm, "mid": v(0.22, -19.54) * mm, "end": v(0.47, -19.97) * mm});
            skArc(sketch, "E15.34.18.0", {"start": v(0, -19) * mm, "mid": v(0, -19.05) * mm, "end": v(0.02, -19.1) * mm});
            skLineSegment(sketch, "E15.38.18.0", {"start": v(0, -19) * mm, "end": v(0, -18.24) * mm});
            skArc(sketch, "E15.41.18.0", {"start": v(0, -18.24) * mm, "mid": v(-0.07, -18.06) * mm, "end": v(-0.25, -17.98) * mm});
            skArc(sketch, "E15.2.19.0", {"start": v(4.9, -17.3) * mm, "mid": v(4.74, -17.42) * mm, "end": v(4.72, -17.61) * mm});
            skLineSegment(sketch, "E15.4.19.0", {"start": v(4.92, -18.35) * mm, "end": v(4.72, -17.61) * mm});
            skArc(sketch, "E15.7.19.0", {"start": v(4.92, -18.35) * mm, "mid": v(4.93, -18.4) * mm, "end": v(4.93, -18.45) * mm});
            skArc(sketch, "E15.11.19.0", {"start": v(4.93, -18.45) * mm, "mid": v(4.84, -18.94) * mm, "end": v(4.71, -19.41) * mm});
            skArc(sketch, "E15.15.19.0", {"start": v(4.71, -19.41) * mm, "mid": v(4.64, -19.51) * mm, "end": v(4.54, -19.58) * mm});
            skLineSegment(sketch, "E15.19.19.0", {"start": v(4.54, -19.58) * mm, "end": v(4.35, -19.62) * mm});
            skLineSegment(sketch, "E15.22.19.0", {"start": v(4.16, -19.66) * mm, "end": v(4.35, -19.62) * mm});
            skPoint(sketch, "E15.25.19.0", {"position": v(4.03, -19.68) * mm});
            skArc(sketch, "E15.26.19.0", {"start": v(3.93, -19.58) * mm, "mid": v(4.04, -19.65) * mm, "end": v(4.16, -19.66) * mm});
            skArc(sketch, "E15.30.19.0", {"start": v(3.33, -18.8) * mm, "mid": v(3.61, -19.2) * mm, "end": v(3.93, -19.58) * mm});
            skArc(sketch, "E15.34.19.0", {"start": v(3.3, -18.71) * mm, "mid": v(3.31, -18.76) * mm, "end": v(3.33, -18.8) * mm});
            skLineSegment(sketch, "E15.38.19.0", {"start": v(3.3, -18.71) * mm, "end": v(3.17, -17.96) * mm});
            skArc(sketch, "E15.41.19.0", {"start": v(3.17, -17.96) * mm, "mid": v(3.06, -17.8) * mm, "end": v(2.88, -17.75) * mm});
            skArc(sketch, "E15.2.20.0", {"start": v(7.83, -16.2) * mm, "mid": v(7.7, -16.33) * mm, "end": v(7.7, -16.53) * mm});
            skLineSegment(sketch, "E15.4.20.0", {"start": v(8.03, -17.22) * mm, "end": v(7.7, -16.53) * mm});
            skArc(sketch, "E15.7.20.0", {"start": v(8.03, -17.22) * mm, "mid": v(8.05, -17.27) * mm, "end": v(8.05, -17.31) * mm});
            skArc(sketch, "E15.11.20.0", {"start": v(8.05, -17.31) * mm, "mid": v(8.06, -17.8) * mm, "end": v(8, -18.3) * mm});
            skArc(sketch, "E15.15.20.0", {"start": v(8, -18.3) * mm, "mid": v(7.96, -18.41) * mm, "end": v(7.87, -18.5) * mm});
            skLineSegment(sketch, "E15.19.20.0", {"start": v(7.87, -18.5) * mm, "end": v(7.7, -18.57) * mm});
            skLineSegment(sketch, "E15.22.20.0", {"start": v(7.51, -18.64) * mm, "end": v(7.7, -18.57) * mm});
            skPoint(sketch, "E15.25.20.0", {"position": v(7.39, -18.68) * mm});
            skArc(sketch, "E15.26.20.0", {"start": v(7.27, -18.6) * mm, "mid": v(7.39, -18.65) * mm, "end": v(7.51, -18.64) * mm});
            skArc(sketch, "E15.30.20.0", {"start": v(6.55, -17.94) * mm, "mid": v(6.9, -18.29) * mm, "end": v(7.27, -18.6) * mm});
            skArc(sketch, "E15.34.20.0", {"start": v(6.5, -17.86) * mm, "mid": v(6.52, -17.9) * mm, "end": v(6.55, -17.94) * mm});
            skLineSegment(sketch, "E15.38.20.0", {"start": v(6.5, -17.86) * mm, "end": v(6.24, -17.14) * mm});
            skArc(sketch, "E15.41.20.0", {"start": v(6.24, -17.14) * mm, "mid": v(6.1, -17) * mm, "end": v(5.91, -16.98) * mm});
            skArc(sketch, "E15.2.21.0", {"start": v(10.52, -14.59) * mm, "mid": v(10.42, -14.75) * mm, "end": v(10.46, -14.94) * mm});
            skLineSegment(sketch, "E15.4.21.0", {"start": v(10.9, -15.57) * mm, "end": v(10.46, -14.94) * mm});
            skArc(sketch, "E15.7.21.0", {"start": v(10.9, -15.57) * mm, "mid": v(10.92, -15.6) * mm, "end": v(10.94, -15.65) * mm});
            skArc(sketch, "E15.11.21.0", {"start": v(10.94, -15.65) * mm, "mid": v(11.03, -16.14) * mm, "end": v(11.07, -16.63) * mm});
            skArc(sketch, "E15.15.21.0", {"start": v(11.07, -16.63) * mm, "mid": v(11.04, -16.75) * mm, "end": v(10.96, -16.84) * mm});
            skLineSegment(sketch, "E15.19.21.0", {"start": v(10.96, -16.84) * mm, "end": v(10.8, -16.95) * mm});
            skLineSegment(sketch, "E15.22.21.0", {"start": v(10.63, -17.05) * mm, "end": v(10.8, -16.95) * mm});
            skPoint(sketch, "E15.25.21.0", {"position": v(10.52, -17.12) * mm});
            skArc(sketch, "E15.26.21.0", {"start": v(10.4, -17.06) * mm, "mid": v(10.52, -17.08) * mm, "end": v(10.63, -17.05) * mm});
            skArc(sketch, "E15.30.21.0", {"start": v(9.56, -16.53) * mm, "mid": v(9.97, -16.81) * mm, "end": v(10.4, -17.06) * mm});
            skArc(sketch, "E15.34.21.0", {"start": v(9.5, -16.46) * mm, "mid": v(9.53, -16.5) * mm, "end": v(9.56, -16.53) * mm});
            skLineSegment(sketch, "E15.38.21.0", {"start": v(9.5, -16.46) * mm, "end": v(9.12, -15.8) * mm});
            skArc(sketch, "E15.41.21.0", {"start": v(9.12, -15.8) * mm, "mid": v(8.97, -15.67) * mm, "end": v(8.77, -15.7) * mm});
            skArc(sketch, "E15.2.22.0", {"start": v(12.9, -12.54) * mm, "mid": v(12.82, -12.72) * mm, "end": v(12.9, -12.9) * mm});
            skLineSegment(sketch, "E15.4.22.0", {"start": v(13.44, -13.44) * mm, "end": v(12.9, -12.9) * mm});
            skArc(sketch, "E15.7.22.0", {"start": v(13.44, -13.44) * mm, "mid": v(13.47, -13.47) * mm, "end": v(13.5, -13.52) * mm});
            skArc(sketch, "E15.11.22.0", {"start": v(13.5, -13.52) * mm, "mid": v(13.66, -13.98) * mm, "end": v(13.78, -14.45) * mm});
            skArc(sketch, "E15.15.22.0", {"start": v(13.78, -14.45) * mm, "mid": v(13.78, -14.58) * mm, "end": v(13.72, -14.68) * mm});
            skLineSegment(sketch, "E15.19.22.0", {"start": v(13.72, -14.68) * mm, "end": v(13.58, -14.82) * mm});
            skLineSegment(sketch, "E15.22.22.0", {"start": v(13.43, -14.94) * mm, "end": v(13.58, -14.82) * mm});
            skPoint(sketch, "E15.25.22.0", {"position": v(13.33, -15.03) * mm});
            skArc(sketch, "E15.26.22.0", {"start": v(13.2, -15) * mm, "mid": v(13.32, -15) * mm, "end": v(13.43, -14.94) * mm});
            skArc(sketch, "E15.30.22.0", {"start": v(12.29, -14.62) * mm, "mid": v(12.73, -14.83) * mm, "end": v(13.2, -15) * mm});
            skArc(sketch, "E15.34.22.0", {"start": v(12.21, -14.56) * mm, "mid": v(12.25, -14.6) * mm, "end": v(12.29, -14.62) * mm});
            skLineSegment(sketch, "E15.38.22.0", {"start": v(12.21, -14.56) * mm, "end": v(11.72, -13.97) * mm});
            skArc(sketch, "E15.41.22.0", {"start": v(11.72, -13.97) * mm, "mid": v(11.55, -13.88) * mm, "end": v(11.37, -13.94) * mm});
            skArc(sketch, "E15.2.23.0", {"start": v(14.87, -10.1) * mm, "mid": v(14.83, -10.3) * mm, "end": v(14.94, -10.46) * mm});
            skLineSegment(sketch, "E15.4.23.0", {"start": v(15.57, -10.9) * mm, "end": v(14.94, -10.46) * mm});
            skArc(sketch, "E15.7.23.0", {"start": v(15.57, -10.9) * mm, "mid": v(15.6, -10.93) * mm, "end": v(15.63, -10.97) * mm});
            skArc(sketch, "E15.11.23.0", {"start": v(15.63, -10.97) * mm, "mid": v(15.88, -11.4) * mm, "end": v(16.09, -11.84) * mm});
            skArc(sketch, "E15.15.23.0", {"start": v(16.09, -11.84) * mm, "mid": v(16.1, -11.96) * mm, "end": v(16.06, -12.08) * mm});
            skLineSegment(sketch, "E15.19.23.0", {"start": v(16.06, -12.08) * mm, "end": v(15.95, -12.24) * mm});
            skLineSegment(sketch, "E15.22.23.0", {"start": v(15.82, -12.38) * mm, "end": v(15.95, -12.24) * mm});
            skPoint(sketch, "E15.25.23.0", {"position": v(15.74, -12.49) * mm});
            skArc(sketch, "E15.26.23.0", {"start": v(15.6, -12.47) * mm, "mid": v(15.72, -12.46) * mm, "end": v(15.82, -12.38) * mm});
            skArc(sketch, "E15.30.23.0", {"start": v(14.64, -12.26) * mm, "mid": v(15.11, -12.4) * mm, "end": v(15.6, -12.47) * mm});
            skArc(sketch, "E15.34.23.0", {"start": v(14.56, -12.21) * mm, "mid": v(14.6, -12.24) * mm, "end": v(14.64, -12.26) * mm});
            skLineSegment(sketch, "E15.38.23.0", {"start": v(14.56, -12.21) * mm, "end": v(13.97, -11.72) * mm});
            skArc(sketch, "E15.41.23.0", {"start": v(13.97, -11.72) * mm, "mid": v(13.79, -11.66) * mm, "end": v(13.61, -11.75) * mm});
            skArc(sketch, "E15.2.24.0", {"start": v(16.4, -7.37) * mm, "mid": v(16.4, -7.56) * mm, "end": v(16.53, -7.7) * mm});
            skLineSegment(sketch, "E15.4.24.0", {"start": v(17.22, -8.03) * mm, "end": v(16.53, -7.7) * mm});
            skArc(sketch, "E15.7.24.0", {"start": v(17.22, -8.03) * mm, "mid": v(17.26, -8.05) * mm, "end": v(17.3, -8.09) * mm});
            skArc(sketch, "E15.11.24.0", {"start": v(17.3, -8.09) * mm, "mid": v(17.62, -8.46) * mm, "end": v(17.9, -8.87) * mm});
            skArc(sketch, "E15.15.24.0", {"start": v(17.9, -8.87) * mm, "mid": v(17.93, -8.99) * mm, "end": v(17.91, -9.1) * mm});
            skLineSegment(sketch, "E15.19.24.0", {"start": v(17.91, -9.1) * mm, "end": v(17.83, -9.28) * mm});
            skLineSegment(sketch, "E15.22.24.0", {"start": v(17.73, -9.45) * mm, "end": v(17.83, -9.28) * mm});
            skPoint(sketch, "E15.25.24.0", {"position": v(17.67, -9.56) * mm});
            skArc(sketch, "E15.26.24.0", {"start": v(17.53, -9.57) * mm, "mid": v(17.65, -9.54) * mm, "end": v(17.73, -9.45) * mm});
            skArc(sketch, "E15.30.24.0", {"start": v(16.55, -9.53) * mm, "mid": v(17.04, -9.58) * mm, "end": v(17.53, -9.57) * mm});
            skArc(sketch, "E15.34.24.0", {"start": v(16.46, -9.5) * mm, "mid": v(16.5, -9.52) * mm, "end": v(16.55, -9.53) * mm});
            skLineSegment(sketch, "E15.38.24.0", {"start": v(16.46, -9.5) * mm, "end": v(15.8, -9.12) * mm});
            skArc(sketch, "E15.41.24.0", {"start": v(15.8, -9.12) * mm, "mid": v(15.6, -9.1) * mm, "end": v(15.45, -9.2) * mm});
            skArc(sketch, "E15.2.25.0", {"start": v(17.43, -4.41) * mm, "mid": v(17.46, -4.6) * mm, "end": v(17.61, -4.72) * mm});
            skLineSegment(sketch, "E15.4.25.0", {"start": v(18.35, -4.92) * mm, "end": v(17.61, -4.72) * mm});
            skArc(sketch, "E15.7.25.0", {"start": v(18.35, -4.92) * mm, "mid": v(18.4, -4.93) * mm, "end": v(18.44, -4.96) * mm});
            skArc(sketch, "E15.11.25.0", {"start": v(18.44, -4.96) * mm, "mid": v(18.82, -5.27) * mm, "end": v(19.17, -5.63) * mm});
            skArc(sketch, "E15.15.25.0", {"start": v(19.17, -5.63) * mm, "mid": v(19.22, -5.74) * mm, "end": v(19.22, -5.86) * mm});
            skLineSegment(sketch, "E15.19.25.0", {"start": v(19.22, -5.86) * mm, "end": v(19.17, -6.04) * mm});
            skLineSegment(sketch, "E15.22.25.0", {"start": v(19.1, -6.22) * mm, "end": v(19.17, -6.04) * mm});
            skPoint(sketch, "E15.25.25.0", {"position": v(19.06, -6.35) * mm});
            skArc(sketch, "E15.26.25.0", {"start": v(18.93, -6.38) * mm, "mid": v(19.04, -6.33) * mm, "end": v(19.1, -6.22) * mm});
            skArc(sketch, "E15.30.25.0", {"start": v(17.95, -6.51) * mm, "mid": v(18.44, -6.47) * mm, "end": v(18.93, -6.38) * mm});
            skArc(sketch, "E15.34.25.0", {"start": v(17.86, -6.5) * mm, "mid": v(17.9, -6.51) * mm, "end": v(17.95, -6.51) * mm});
            skLineSegment(sketch, "E15.38.25.0", {"start": v(17.86, -6.5) * mm, "end": v(17.14, -6.24) * mm});
            skArc(sketch, "E15.41.25.0", {"start": v(17.14, -6.24) * mm, "mid": v(16.94, -6.24) * mm, "end": v(16.81, -6.39) * mm});
            skArc(sketch, "E15.2.26.0", {"start": v(17.93, -1.32) * mm, "mid": v(18, -1.5) * mm, "end": v(18.17, -1.59) * mm});
            skLineSegment(sketch, "E15.4.26.0", {"start": v(18.93, -1.66) * mm, "end": v(18.17, -1.59) * mm});
            skArc(sketch, "E15.7.26.0", {"start": v(18.93, -1.66) * mm, "mid": v(18.98, -1.66) * mm, "end": v(19.02, -1.68) * mm});
            skArc(sketch, "E15.11.26.0", {"start": v(19.02, -1.68) * mm, "mid": v(19.45, -1.93) * mm, "end": v(19.85, -2.21) * mm});
            skArc(sketch, "E15.15.26.0", {"start": v(19.85, -2.21) * mm, "mid": v(19.93, -2.31) * mm, "end": v(19.95, -2.43) * mm});
            skLineSegment(sketch, "E15.19.26.0", {"start": v(19.95, -2.43) * mm, "end": v(19.93, -2.62) * mm});
            skLineSegment(sketch, "E15.22.26.0", {"start": v(19.9, -2.81) * mm, "end": v(19.93, -2.62) * mm});
            skPoint(sketch, "E15.25.26.0", {"position": v(19.87, -2.94) * mm});
            skArc(sketch, "E15.26.26.0", {"start": v(19.75, -3) * mm, "mid": v(19.85, -2.93) * mm, "end": v(19.9, -2.81) * mm});
            skArc(sketch, "E15.30.26.0", {"start": v(18.8, -3.3) * mm, "mid": v(19.29, -3.17) * mm, "end": v(19.75, -3) * mm});
            skArc(sketch, "E15.34.26.0", {"start": v(18.71, -3.3) * mm, "mid": v(18.76, -3.3) * mm, "end": v(18.8, -3.3) * mm});
            skLineSegment(sketch, "E15.38.26.0", {"start": v(18.71, -3.3) * mm, "end": v(17.96, -3.17) * mm});
            skArc(sketch, "E15.41.26.0", {"start": v(17.96, -3.17) * mm, "mid": v(17.77, -3.2) * mm, "end": v(17.66, -3.37) * mm});
            skArc(sketch, "E15.2.27.0", {"start": v(17.9, 1.82) * mm, "mid": v(17.98, 1.65) * mm, "end": v(18.17, 1.59) * mm});
            skLineSegment(sketch, "E15.4.27.0", {"start": v(18.93, 1.66) * mm, "end": v(18.17, 1.59) * mm});
            skArc(sketch, "E15.7.27.0", {"start": v(18.93, 1.66) * mm, "mid": v(18.98, 1.66) * mm, "end": v(19.02, 1.65) * mm});
            skArc(sketch, "E15.11.27.0", {"start": v(19.02, 1.65) * mm, "mid": v(19.49, 1.48) * mm, "end": v(19.93, 1.27) * mm});
            skArc(sketch, "E15.15.27.0", {"start": v(19.93, 1.27) * mm, "mid": v(20.02, 1.18) * mm, "end": v(20.07, 1.07) * mm});
            skLineSegment(sketch, "E15.19.27.0", {"start": v(20.07, 1.07) * mm, "end": v(20.08, 0.88) * mm});
            skLineSegment(sketch, "E15.22.27.0", {"start": v(20.08, 0.69) * mm, "end": v(20.08, 0.88) * mm});
            skPoint(sketch, "E15.25.27.0", {"position": v(20.08, 0.55) * mm});
            skArc(sketch, "E15.26.27.0", {"start": v(19.97, 0.47) * mm, "mid": v(20.05, 0.56) * mm, "end": v(20.08, 0.69) * mm});
            skArc(sketch, "E15.30.27.0", {"start": v(19.1, 0.02) * mm, "mid": v(19.54, 0.22) * mm, "end": v(19.97, 0.47) * mm});
            skArc(sketch, "E15.34.27.0", {"start": v(19, 0) * mm, "mid": v(19.05, 0) * mm, "end": v(19.1, 0.02) * mm});
            skLineSegment(sketch, "E15.38.27.0", {"start": v(19, 0) * mm, "end": v(18.24, 0) * mm});
            skArc(sketch, "E15.41.27.0", {"start": v(18.24, 0) * mm, "mid": v(18.06, -0.07) * mm, "end": v(17.98, -0.25) * mm});
            skArc(sketch, "E15.2.28.0", {"start": v(17.3, 4.9) * mm, "mid": v(17.42, 4.74) * mm, "end": v(17.61, 4.72) * mm});
            skLineSegment(sketch, "E15.4.28.0", {"start": v(18.35, 4.92) * mm, "end": v(17.61, 4.72) * mm});
            skArc(sketch, "E15.7.28.0", {"start": v(18.35, 4.92) * mm, "mid": v(18.4, 4.93) * mm, "end": v(18.45, 4.93) * mm});
            skArc(sketch, "E15.11.28.0", {"start": v(18.45, 4.93) * mm, "mid": v(18.94, 4.84) * mm, "end": v(19.41, 4.71) * mm});
            skArc(sketch, "E15.15.28.0", {"start": v(19.41, 4.71) * mm, "mid": v(19.51, 4.64) * mm, "end": v(19.58, 4.54) * mm});
            skLineSegment(sketch, "E15.19.28.0", {"start": v(19.58, 4.54) * mm, "end": v(19.62, 4.35) * mm});
            skLineSegment(sketch, "E15.22.28.0", {"start": v(19.66, 4.16) * mm, "end": v(19.62, 4.35) * mm});
            skPoint(sketch, "E15.25.28.0", {"position": v(19.68, 4.03) * mm});
            skArc(sketch, "E15.26.28.0", {"start": v(19.58, 3.93) * mm, "mid": v(19.65, 4.04) * mm, "end": v(19.66, 4.16) * mm});
            skArc(sketch, "E15.30.28.0", {"start": v(18.8, 3.33) * mm, "mid": v(19.2, 3.61) * mm, "end": v(19.58, 3.93) * mm});
            skArc(sketch, "E15.34.28.0", {"start": v(18.71, 3.3) * mm, "mid": v(18.76, 3.31) * mm, "end": v(18.8, 3.33) * mm});
            skLineSegment(sketch, "E15.38.28.0", {"start": v(18.71, 3.3) * mm, "end": v(17.96, 3.17) * mm});
            skArc(sketch, "E15.41.28.0", {"start": v(17.96, 3.17) * mm, "mid": v(17.8, 3.06) * mm, "end": v(17.75, 2.88) * mm});
            skArc(sketch, "E15.2.29.0", {"start": v(16.2, 7.83) * mm, "mid": v(16.33, 7.7) * mm, "end": v(16.53, 7.7) * mm});
            skLineSegment(sketch, "E15.4.29.0", {"start": v(17.22, 8.03) * mm, "end": v(16.53, 7.7) * mm});
            skArc(sketch, "E15.7.29.0", {"start": v(17.22, 8.03) * mm, "mid": v(17.27, 8.05) * mm, "end": v(17.31, 8.05) * mm});
            skArc(sketch, "E15.11.29.0", {"start": v(17.31, 8.05) * mm, "mid": v(17.8, 8.06) * mm, "end": v(18.3, 8) * mm});
            skArc(sketch, "E15.15.29.0", {"start": v(18.3, 8) * mm, "mid": v(18.41, 7.96) * mm, "end": v(18.5, 7.87) * mm});
            skLineSegment(sketch, "E15.19.29.0", {"start": v(18.5, 7.87) * mm, "end": v(18.57, 7.7) * mm});
            skLineSegment(sketch, "E15.22.29.0", {"start": v(18.64, 7.51) * mm, "end": v(18.57, 7.7) * mm});
            skPoint(sketch, "E15.25.29.0", {"position": v(18.68, 7.39) * mm});
            skArc(sketch, "E15.26.29.0", {"start": v(18.6, 7.27) * mm, "mid": v(18.65, 7.39) * mm, "end": v(18.64, 7.51) * mm});
            skArc(sketch, "E15.30.29.0", {"start": v(17.94, 6.55) * mm, "mid": v(18.29, 6.9) * mm, "end": v(18.6, 7.27) * mm});
            skArc(sketch, "E15.34.29.0", {"start": v(17.86, 6.5) * mm, "mid": v(17.9, 6.52) * mm, "end": v(17.94, 6.55) * mm});
            skLineSegment(sketch, "E15.38.29.0", {"start": v(17.86, 6.5) * mm, "end": v(17.14, 6.24) * mm});
            skArc(sketch, "E15.41.29.0", {"start": v(17.14, 6.24) * mm, "mid": v(17, 6.1) * mm, "end": v(16.98, 5.91) * mm});
            skArc(sketch, "E15.2.30.0", {"start": v(14.59, 10.52) * mm, "mid": v(14.75, 10.42) * mm, "end": v(14.94, 10.46) * mm});
            skLineSegment(sketch, "E15.4.30.0", {"start": v(15.57, 10.9) * mm, "end": v(14.94, 10.46) * mm});
            skArc(sketch, "E15.7.30.0", {"start": v(15.57, 10.9) * mm, "mid": v(15.6, 10.92) * mm, "end": v(15.65, 10.94) * mm});
            skArc(sketch, "E15.11.30.0", {"start": v(15.65, 10.94) * mm, "mid": v(16.14, 11.03) * mm, "end": v(16.63, 11.07) * mm});
            skArc(sketch, "E15.15.30.0", {"start": v(16.63, 11.07) * mm, "mid": v(16.75, 11.04) * mm, "end": v(16.84, 10.96) * mm});
            skLineSegment(sketch, "E15.19.30.0", {"start": v(16.84, 10.96) * mm, "end": v(16.95, 10.8) * mm});
            skLineSegment(sketch, "E15.22.30.0", {"start": v(17.05, 10.63) * mm, "end": v(16.95, 10.8) * mm});
            skPoint(sketch, "E15.25.30.0", {"position": v(17.12, 10.52) * mm});
            skArc(sketch, "E15.26.30.0", {"start": v(17.06, 10.4) * mm, "mid": v(17.08, 10.52) * mm, "end": v(17.05, 10.63) * mm});
            skArc(sketch, "E15.30.30.0", {"start": v(16.53, 9.56) * mm, "mid": v(16.81, 9.97) * mm, "end": v(17.06, 10.4) * mm});
            skArc(sketch, "E15.34.30.0", {"start": v(16.46, 9.5) * mm, "mid": v(16.5, 9.53) * mm, "end": v(16.53, 9.56) * mm});
            skLineSegment(sketch, "E15.38.30.0", {"start": v(16.46, 9.5) * mm, "end": v(15.8, 9.12) * mm});
            skArc(sketch, "E15.41.30.0", {"start": v(15.8, 9.12) * mm, "mid": v(15.67, 8.97) * mm, "end": v(15.7, 8.77) * mm});
            skArc(sketch, "E15.2.31.0", {"start": v(12.54, 12.9) * mm, "mid": v(12.72, 12.82) * mm, "end": v(12.9, 12.9) * mm});
            skLineSegment(sketch, "E15.4.31.0", {"start": v(13.44, 13.44) * mm, "end": v(12.9, 12.9) * mm});
            skArc(sketch, "E15.7.31.0", {"start": v(13.44, 13.44) * mm, "mid": v(13.47, 13.47) * mm, "end": v(13.52, 13.5) * mm});
            skArc(sketch, "E15.11.31.0", {"start": v(13.52, 13.5) * mm, "mid": v(13.98, 13.66) * mm, "end": v(14.45, 13.78) * mm});
            skArc(sketch, "E15.15.31.0", {"start": v(14.45, 13.78) * mm, "mid": v(14.58, 13.78) * mm, "end": v(14.68, 13.72) * mm});
            skLineSegment(sketch, "E15.19.31.0", {"start": v(14.68, 13.72) * mm, "end": v(14.82, 13.58) * mm});
            skLineSegment(sketch, "E15.22.31.0", {"start": v(14.94, 13.43) * mm, "end": v(14.82, 13.58) * mm});
            skPoint(sketch, "E15.25.31.0", {"position": v(15.03, 13.33) * mm});
            skArc(sketch, "E15.26.31.0", {"start": v(15, 13.2) * mm, "mid": v(15, 13.32) * mm, "end": v(14.94, 13.43) * mm});
            skArc(sketch, "E15.30.31.0", {"start": v(14.62, 12.29) * mm, "mid": v(14.83, 12.73) * mm, "end": v(15, 13.2) * mm});
            skArc(sketch, "E15.34.31.0", {"start": v(14.56, 12.21) * mm, "mid": v(14.6, 12.25) * mm, "end": v(14.62, 12.29) * mm});
            skLineSegment(sketch, "E15.38.31.0", {"start": v(14.56, 12.21) * mm, "end": v(13.97, 11.72) * mm});
            skArc(sketch, "E15.41.31.0", {"start": v(13.97, 11.72) * mm, "mid": v(13.88, 11.55) * mm, "end": v(13.94, 11.37) * mm});
            skArc(sketch, "E15.2.32.0", {"start": v(10.1, 14.87) * mm, "mid": v(10.3, 14.83) * mm, "end": v(10.46, 14.94) * mm});
            skLineSegment(sketch, "E15.4.32.0", {"start": v(10.9, 15.57) * mm, "end": v(10.46, 14.94) * mm});
            skArc(sketch, "E15.7.32.0", {"start": v(10.9, 15.57) * mm, "mid": v(10.93, 15.6) * mm, "end": v(10.97, 15.63) * mm});
            skArc(sketch, "E15.11.32.0", {"start": v(10.97, 15.63) * mm, "mid": v(11.4, 15.88) * mm, "end": v(11.84, 16.09) * mm});
            skArc(sketch, "E15.15.32.0", {"start": v(11.84, 16.09) * mm, "mid": v(11.96, 16.1) * mm, "end": v(12.08, 16.06) * mm});
            skLineSegment(sketch, "E15.19.32.0", {"start": v(12.08, 16.06) * mm, "end": v(12.24, 15.95) * mm});
            skLineSegment(sketch, "E15.22.32.0", {"start": v(12.38, 15.82) * mm, "end": v(12.24, 15.95) * mm});
            skPoint(sketch, "E15.25.32.0", {"position": v(12.49, 15.74) * mm});
            skArc(sketch, "E15.26.32.0", {"start": v(12.47, 15.6) * mm, "mid": v(12.46, 15.72) * mm, "end": v(12.38, 15.82) * mm});
            skArc(sketch, "E15.30.32.0", {"start": v(12.26, 14.64) * mm, "mid": v(12.4, 15.11) * mm, "end": v(12.47, 15.6) * mm});
            skArc(sketch, "E15.34.32.0", {"start": v(12.21, 14.56) * mm, "mid": v(12.24, 14.6) * mm, "end": v(12.26, 14.64) * mm});
            skLineSegment(sketch, "E15.38.32.0", {"start": v(12.21, 14.56) * mm, "end": v(11.72, 13.97) * mm});
            skArc(sketch, "E15.41.32.0", {"start": v(11.72, 13.97) * mm, "mid": v(11.66, 13.79) * mm, "end": v(11.75, 13.61) * mm});
            skArc(sketch, "E15.2.33.0", {"start": v(7.37, 16.4) * mm, "mid": v(7.56, 16.4) * mm, "end": v(7.7, 16.53) * mm});
            skLineSegment(sketch, "E15.4.33.0", {"start": v(8.03, 17.22) * mm, "end": v(7.7, 16.53) * mm});
            skArc(sketch, "E15.7.33.0", {"start": v(8.03, 17.22) * mm, "mid": v(8.05, 17.26) * mm, "end": v(8.09, 17.3) * mm});
            skArc(sketch, "E15.11.33.0", {"start": v(8.09, 17.3) * mm, "mid": v(8.46, 17.62) * mm, "end": v(8.87, 17.9) * mm});
            skArc(sketch, "E15.15.33.0", {"start": v(8.87, 17.9) * mm, "mid": v(8.99, 17.93) * mm, "end": v(9.1, 17.91) * mm});
            skLineSegment(sketch, "E15.19.33.0", {"start": v(9.1, 17.91) * mm, "end": v(9.28, 17.83) * mm});
            skLineSegment(sketch, "E15.22.33.0", {"start": v(9.45, 17.73) * mm, "end": v(9.28, 17.83) * mm});
            skPoint(sketch, "E15.25.33.0", {"position": v(9.56, 17.67) * mm});
            skArc(sketch, "E15.26.33.0", {"start": v(9.57, 17.53) * mm, "mid": v(9.54, 17.65) * mm, "end": v(9.45, 17.73) * mm});
            skArc(sketch, "E15.30.33.0", {"start": v(9.53, 16.55) * mm, "mid": v(9.58, 17.04) * mm, "end": v(9.57, 17.53) * mm});
            skArc(sketch, "E15.34.33.0", {"start": v(9.5, 16.46) * mm, "mid": v(9.52, 16.5) * mm, "end": v(9.53, 16.55) * mm});
            skLineSegment(sketch, "E15.38.33.0", {"start": v(9.5, 16.46) * mm, "end": v(9.12, 15.8) * mm});
            skArc(sketch, "E15.41.33.0", {"start": v(9.12, 15.8) * mm, "mid": v(9.1, 15.6) * mm, "end": v(9.2, 15.45) * mm});
            skArc(sketch, "E15.2.34.0", {"start": v(4.41, 17.43) * mm, "mid": v(4.6, 17.46) * mm, "end": v(4.72, 17.61) * mm});
            skLineSegment(sketch, "E15.4.34.0", {"start": v(4.92, 18.35) * mm, "end": v(4.72, 17.61) * mm});
            skArc(sketch, "E15.7.34.0", {"start": v(4.92, 18.35) * mm, "mid": v(4.93, 18.4) * mm, "end": v(4.96, 18.44) * mm});
            skArc(sketch, "E15.11.34.0", {"start": v(4.96, 18.44) * mm, "mid": v(5.27, 18.82) * mm, "end": v(5.63, 19.17) * mm});
            skArc(sketch, "E15.15.34.0", {"start": v(5.63, 19.17) * mm, "mid": v(5.74, 19.22) * mm, "end": v(5.86, 19.22) * mm});
            skLineSegment(sketch, "E15.19.34.0", {"start": v(5.86, 19.22) * mm, "end": v(6.04, 19.17) * mm});
            skLineSegment(sketch, "E15.22.34.0", {"start": v(6.22, 19.1) * mm, "end": v(6.04, 19.17) * mm});
            skPoint(sketch, "E15.25.34.0", {"position": v(6.35, 19.06) * mm});
            skArc(sketch, "E15.26.34.0", {"start": v(6.38, 18.93) * mm, "mid": v(6.33, 19.04) * mm, "end": v(6.22, 19.1) * mm});
            skArc(sketch, "E15.30.34.0", {"start": v(6.51, 17.95) * mm, "mid": v(6.47, 18.44) * mm, "end": v(6.38, 18.93) * mm});
            skArc(sketch, "E15.34.34.0", {"start": v(6.5, 17.86) * mm, "mid": v(6.51, 17.9) * mm, "end": v(6.51, 17.95) * mm});
            skLineSegment(sketch, "E15.38.34.0", {"start": v(6.5, 17.86) * mm, "end": v(6.24, 17.14) * mm});
            skArc(sketch, "E15.41.34.0", {"start": v(6.24, 17.14) * mm, "mid": v(6.24, 16.94) * mm, "end": v(6.39, 16.81) * mm});
            skArc(sketch, "E15.2.35.0", {"start": v(1.32, 17.93) * mm, "mid": v(1.5, 18) * mm, "end": v(1.59, 18.17) * mm});
            skLineSegment(sketch, "E15.4.35.0", {"start": v(1.66, 18.93) * mm, "end": v(1.59, 18.17) * mm});
            skArc(sketch, "E15.7.35.0", {"start": v(1.66, 18.93) * mm, "mid": v(1.66, 18.98) * mm, "end": v(1.68, 19.02) * mm});
            skArc(sketch, "E15.11.35.0", {"start": v(1.68, 19.02) * mm, "mid": v(1.93, 19.45) * mm, "end": v(2.21, 19.85) * mm});
            skArc(sketch, "E15.15.35.0", {"start": v(2.21, 19.85) * mm, "mid": v(2.31, 19.93) * mm, "end": v(2.43, 19.95) * mm});
            skLineSegment(sketch, "E15.19.35.0", {"start": v(2.43, 19.95) * mm, "end": v(2.62, 19.93) * mm});
            skLineSegment(sketch, "E15.22.35.0", {"start": v(2.81, 19.9) * mm, "end": v(2.62, 19.93) * mm});
            skPoint(sketch, "E15.25.35.0", {"position": v(2.94, 19.87) * mm});
            skArc(sketch, "E15.26.35.0", {"start": v(3, 19.75) * mm, "mid": v(2.93, 19.85) * mm, "end": v(2.81, 19.9) * mm});
            skArc(sketch, "E15.30.35.0", {"start": v(3.3, 18.8) * mm, "mid": v(3.17, 19.29) * mm, "end": v(3, 19.75) * mm});
            skArc(sketch, "E15.34.35.0", {"start": v(3.3, 18.71) * mm, "mid": v(3.3, 18.76) * mm, "end": v(3.3, 18.8) * mm});
            skLineSegment(sketch, "E15.38.35.0", {"start": v(3.3, 18.71) * mm, "end": v(3.17, 17.96) * mm});
            skArc(sketch, "E15.41.35.0", {"start": v(3.17, 17.96) * mm, "mid": v(3.2, 17.77) * mm, "end": v(3.37, 17.66) * mm});
            skArc(sketch, "E16.trimOffspring", {"start": v(1.32, 17.93) * mm, "mid": v(0.78, 17.97) * mm, "end": v(0.25, 17.98) * mm});
            skArc(sketch, "E17.trimOffspring", {"start": v(4.41, 17.43) * mm, "mid": v(3.9, 17.56) * mm, "end": v(3.37, 17.66) * mm});
            skArc(sketch, "E18.trimOffspring", {"start": v(7.37, 16.4) * mm, "mid": v(6.88, 16.61) * mm, "end": v(6.39, 16.81) * mm});
            skArc(sketch, "E19.trimOffspring", {"start": v(10.1, 14.87) * mm, "mid": v(9.66, 15.17) * mm, "end": v(9.2, 15.45) * mm});
            skArc(sketch, "E20.trimOffspring", {"start": v(12.54, 12.9) * mm, "mid": v(12.15, 13.26) * mm, "end": v(11.75, 13.61) * mm});
            skArc(sketch, "E21.trimOffspring", {"start": v(14.59, 10.52) * mm, "mid": v(14.27, 10.95) * mm, "end": v(13.94, 11.37) * mm});
            skArc(sketch, "E22.trimOffspring", {"start": v(16.2, 7.83) * mm, "mid": v(15.95, 8.3) * mm, "end": v(15.7, 8.77) * mm});
            skArc(sketch, "E23.trimOffspring", {"start": v(17.3, 4.9) * mm, "mid": v(17.15, 5.4) * mm, "end": v(16.98, 5.91) * mm});
            skArc(sketch, "E24.trimOffspring", {"start": v(17.9, 1.82) * mm, "mid": v(17.83, 2.35) * mm, "end": v(17.75, 2.88) * mm});
            skArc(sketch, "E25.trimOffspring", {"start": v(17.93, -1.32) * mm, "mid": v(17.97, -0.78) * mm, "end": v(17.98, -0.25) * mm});
            skArc(sketch, "E26.trimOffspring", {"start": v(17.43, -4.41) * mm, "mid": v(17.56, -3.9) * mm, "end": v(17.66, -3.37) * mm});
            skArc(sketch, "E27.trimOffspring", {"start": v(16.4, -7.37) * mm, "mid": v(16.61, -6.88) * mm, "end": v(16.81, -6.39) * mm});
            skArc(sketch, "E28.trimOffspring", {"start": v(14.87, -10.1) * mm, "mid": v(15.17, -9.66) * mm, "end": v(15.45, -9.2) * mm});
            skArc(sketch, "E29.trimOffspring", {"start": v(12.9, -12.54) * mm, "mid": v(13.26, -12.15) * mm, "end": v(13.61, -11.75) * mm});
            skArc(sketch, "E30.trimOffspring", {"start": v(10.52, -14.59) * mm, "mid": v(10.95, -14.27) * mm, "end": v(11.37, -13.94) * mm});
            skArc(sketch, "E31.trimOffspring", {"start": v(7.83, -16.2) * mm, "mid": v(8.3, -15.95) * mm, "end": v(8.77, -15.7) * mm});
            skArc(sketch, "E32.trimOffspring", {"start": v(4.9, -17.3) * mm, "mid": v(5.4, -17.15) * mm, "end": v(5.91, -16.98) * mm});
            skArc(sketch, "E33.trimOffspring", {"start": v(1.82, -17.9) * mm, "mid": v(2.35, -17.83) * mm, "end": v(2.88, -17.75) * mm});
            skArc(sketch, "E34.trimOffspring", {"start": v(-1.32, -17.93) * mm, "mid": v(-0.78, -17.97) * mm, "end": v(-0.25, -17.98) * mm});
            skArc(sketch, "E35.trimOffspring", {"start": v(-4.41, -17.43) * mm, "mid": v(-3.9, -17.56) * mm, "end": v(-3.37, -17.66) * mm});
            skArc(sketch, "E36.trimOffspring", {"start": v(-7.37, -16.4) * mm, "mid": v(-6.88, -16.61) * mm, "end": v(-6.39, -16.81) * mm});
            skArc(sketch, "E37.trimOffspring", {"start": v(-10.1, -14.87) * mm, "mid": v(-9.66, -15.17) * mm, "end": v(-9.2, -15.45) * mm});
            skArc(sketch, "E38.trimOffspring", {"start": v(-12.54, -12.9) * mm, "mid": v(-12.15, -13.26) * mm, "end": v(-11.75, -13.61) * mm});
            skArc(sketch, "E39.trimOffspring", {"start": v(-14.59, -10.52) * mm, "mid": v(-14.27, -10.95) * mm, "end": v(-13.94, -11.37) * mm});
            skArc(sketch, "E40.trimOffspring", {"start": v(-16.2, -7.83) * mm, "mid": v(-15.95, -8.3) * mm, "end": v(-15.7, -8.77) * mm});
            skArc(sketch, "E41.trimOffspring", {"start": v(-17.3, -4.9) * mm, "mid": v(-17.15, -5.4) * mm, "end": v(-16.98, -5.91) * mm});
            skArc(sketch, "E42.trimOffspring", {"start": v(-17.9, -1.82) * mm, "mid": v(-17.83, -2.35) * mm, "end": v(-17.75, -2.88) * mm});
            skArc(sketch, "E43.trimOffspring", {"start": v(-17.93, 1.32) * mm, "mid": v(-17.97, 0.78) * mm, "end": v(-17.98, 0.25) * mm});
            skArc(sketch, "E44.trimOffspring", {"start": v(-17.43, 4.41) * mm, "mid": v(-17.56, 3.9) * mm, "end": v(-17.66, 3.37) * mm});
            skArc(sketch, "E45.trimOffspring", {"start": v(-16.4, 7.37) * mm, "mid": v(-16.61, 6.88) * mm, "end": v(-16.81, 6.39) * mm});
            skArc(sketch, "E46.trimOffspring", {"start": v(-14.87, 10.1) * mm, "mid": v(-15.17, 9.66) * mm, "end": v(-15.45, 9.2) * mm});
            skArc(sketch, "E47.trimOffspring", {"start": v(-12.9, 12.54) * mm, "mid": v(-13.26, 12.15) * mm, "end": v(-13.61, 11.75) * mm});
            skArc(sketch, "E48.trimOffspring", {"start": v(-10.52, 14.59) * mm, "mid": v(-10.95, 14.27) * mm, "end": v(-11.37, 13.94) * mm});
            skArc(sketch, "E49.trimOffspring", {"start": v(-7.83, 16.2) * mm, "mid": v(-8.3, 15.95) * mm, "end": v(-8.77, 15.7) * mm});
            skArc(sketch, "E50.trimOffspring", {"start": v(-4.9, 17.3) * mm, "mid": v(-5.4, 17.15) * mm, "end": v(-5.91, 16.98) * mm});
            skCircle(sketch, "E51", {"center": v(0, 0) * mm, "radius": 6.35 * mm});
            skSolve(sketch);
        }
        {
            var Q0;
            Q0=makeQuery(id+"F0.imprint","IMPRINT",FACE,{"disambiguationData":[TD([[makeQuery(id+"F0.imprint","IMPRINT",EDGE,{"derivedFrom":sQuery(id+"F0.wireOp",EDGE,"E0")}),1.0]])]});
            extrude(context, id + "F1", {"entities" : qUnion([Q0]), "depth" : 6.35 * mm});
        }
    });
